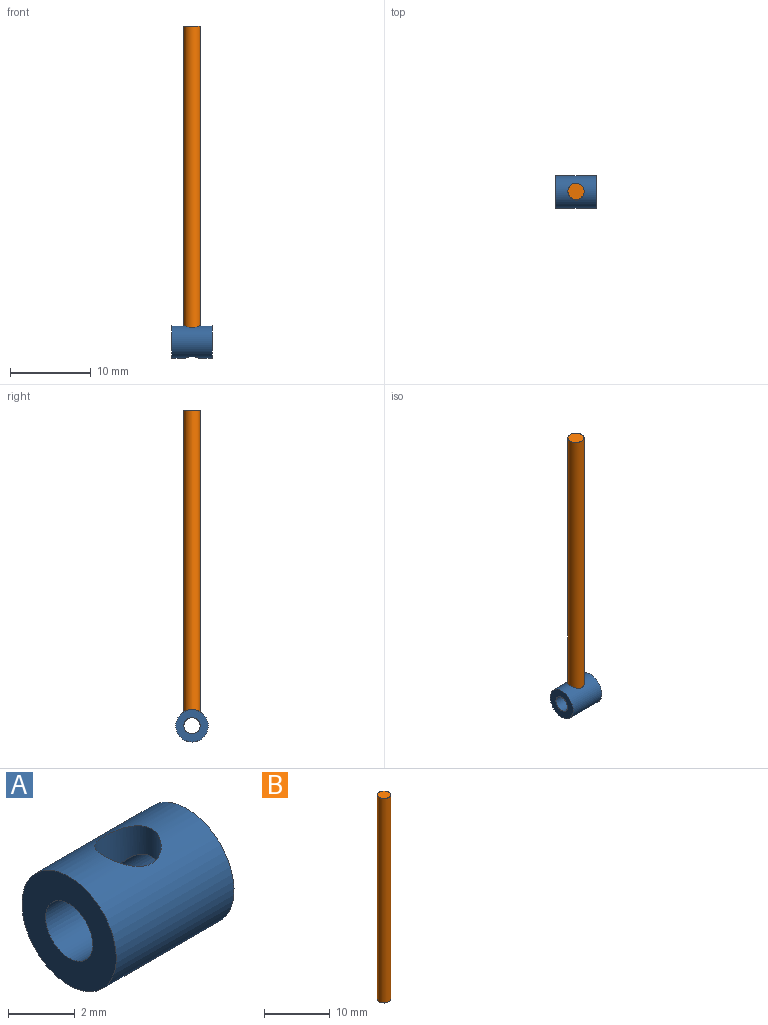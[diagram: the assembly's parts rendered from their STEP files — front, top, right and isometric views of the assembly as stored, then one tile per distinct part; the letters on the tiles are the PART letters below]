
ASSEMBLY  parts=2 mates=1
PART A: 6 faces, bbox 5x4x4 mm
  f0: cylinder r=1mm len=5mm, axis (-1,0,0), area 25.2mm2, adj f2,f3,f4,f5
  f1: cylinder r=2mm len=5mm, axis (-1,0,0), area 57.5mm2, adj f2,f3,f4,f5
  f2: plane 4x4mm, normal (1,0,0), area 9.4mm2, adj f0,f1
  f3: plane 4x4mm, normal (-1,0,0), area 9.4mm2, adj f0,f1
  f4: cylinder r=0.8mm len=1.6mm, axis (0,0,1), area 5.6mm2, adj f0,f1
  f5: cylinder r=1mm len=2mm, axis (0,0,1), area 7.7mm2, adj f0,f1
PART B: 3 faces, bbox 2x2x38 mm
  f0: cylinder r=1mm len=38mm, axis (0,0,-1), area 238.8mm2, adj f1,f2
  f1: plane 2x2mm, normal (0,0,1), area 3.1mm2, adj f0
  f2: plane 2x2mm, normal (0,0,-1), area 3.1mm2, adj f0
PLACE A t=(-1.68,1.04,-19.15)mm
PLACE B t=(0.82,1.04,-18.15)mm
MATE fastened A.f4 <-> B.f0  axis (0,0,1) through (0.82,1.04,-18.15)mm
